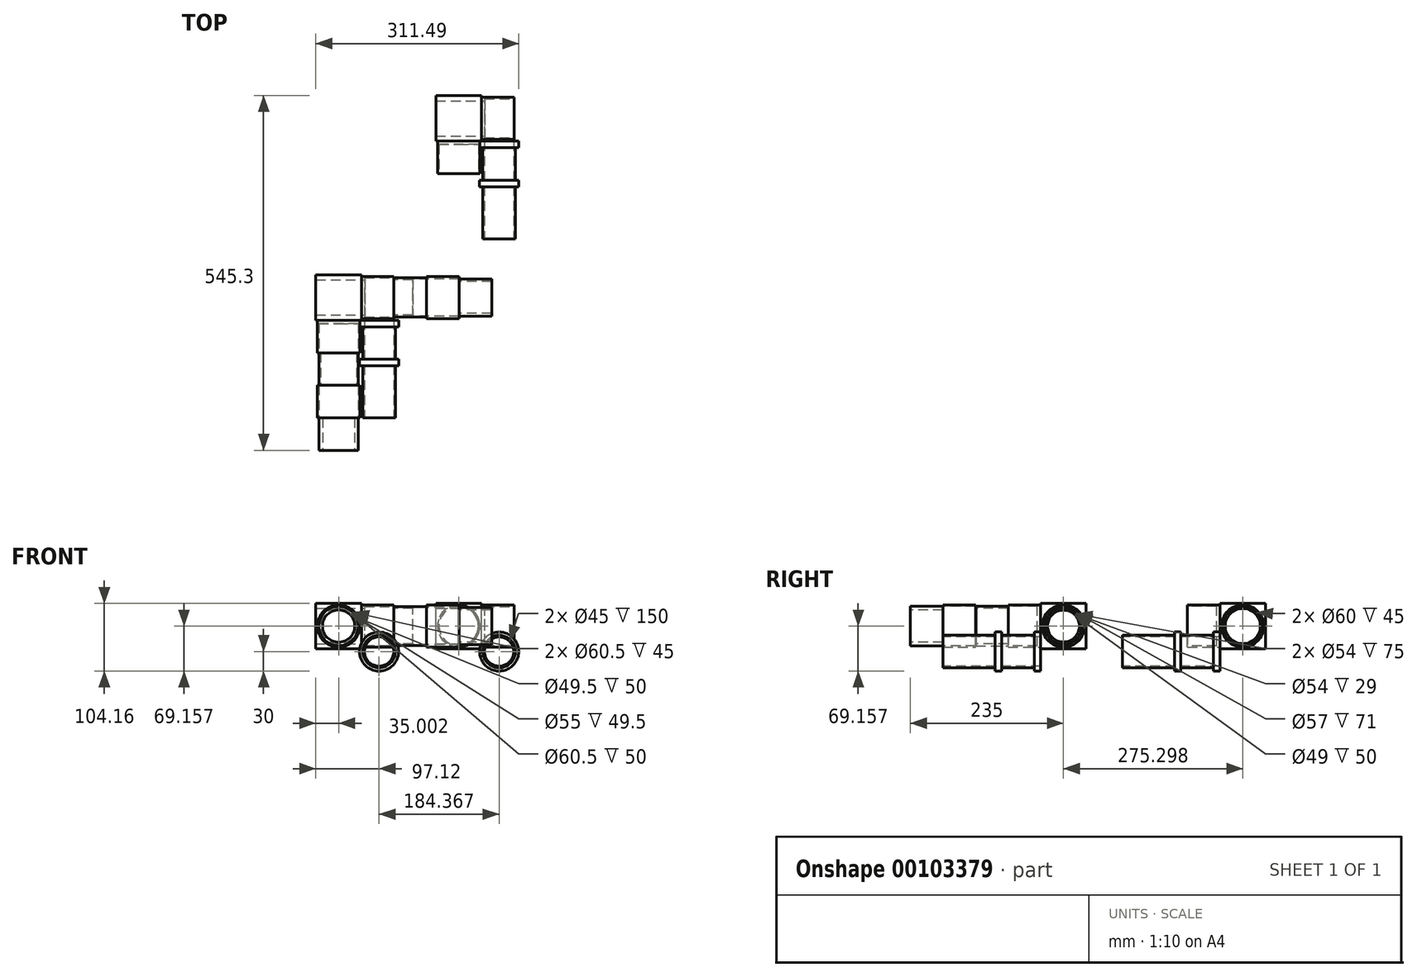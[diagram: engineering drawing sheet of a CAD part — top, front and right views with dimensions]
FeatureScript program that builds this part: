
annotation { "Feature Type Name" : "Feature", "Feature Type Description" : "" }
export const myFeature = defineFeature(function(context is Context, id is Id, definition is map)
    precondition{}
    {
        {
            var Q0;
            Q0=qCreatedBy(makeId("Front.planeOp"),FACE);
            var sketch = newSketch(context, id + "F0", { "sketchPlane" : qUnion([Q0])});
            skCircle(sketch, "E0", {"center": v(0, 0) * mm, "radius": 30 * mm});
            skSolve(sketch);
        }
        {
            var Q0;
            Q0 = qSketchRegion(id + "F0", true);
            extrude(context, id + "F1", {"entities" : qUnion([Q0]), "depth" : 10 * mm});
        }
        {
            var Q0;
            Q0=makeQuery(id+"F1.opExtrude","CAP_FACE",FACE,{"disambiguationData":[OSD([sQuery(id+"F0.wireOp",EDGE,"E0")])],"isStart":false});
            var sketch = newSketch(context, id + "F2", { "sketchPlane" : qUnion([Q0])});
            skCircle(sketch, "E1", {"center": v(0, 0) * mm, "radius": 25 * mm});
            skSolve(sketch);
        }
        {
            var Q0;
            Q0 = qSketchRegion(id + "F2", true);
            extrude(context, id + "F3", {"entities" : qUnion([Q0]), "operationType" : NewBodyOperationType.ADD, "depth" : 50 * mm});
        }
        {
            var Q0;
            Q0=makeQuery(id+"F3.opExtrude","CAP_FACE",FACE,{"disambiguationData":[OSD([sQuery(id+"F2.wireOp",EDGE,"E1")])],"isStart":false});
            var sketch = newSketch(context, id + "F4", { "sketchPlane" : qUnion([Q0])});
            skCircle(sketch, "E2", {"center": v(0, 0) * mm, "radius": 30 * mm});
            skSolve(sketch);
        }
        {
            var Q0;
            Q0 = qSketchRegion(id + "F4", true);
            extrude(context, id + "F5", {"entities" : qUnion([Q0]), "operationType" : NewBodyOperationType.ADD, "depth" : 10 * mm});
        }
        {
            var Q0;
            Q0=makeQuery(id+"F5.opExtrude","CAP_FACE",FACE,{"disambiguationData":[OSD([sQuery(id+"F4.wireOp",EDGE,"E2")])],"isStart":false});
            var sketch = newSketch(context, id + "F6", { "sketchPlane" : qUnion([Q0])});
            skCircle(sketch, "E3", {"center": v(0, 0) * mm, "radius": 25 * mm});
            skSolve(sketch);
        }
        {
            var Q0;
            Q0 = qSketchRegion(id + "F6", true);
            extrude(context, id + "F7", {"entities" : qUnion([Q0]), "operationType" : NewBodyOperationType.ADD, "depth" : 80 * mm});
        }
        {
            var Q0;
            Q0=makeQuery(id+"F7.opExtrude","CAP_FACE",FACE,{"disambiguationData":[OSD([sQuery(id+"F6.wireOp",EDGE,"E3")])],"isStart":false});
            var sketch = newSketch(context, id + "F8", { "sketchPlane" : qUnion([Q0])});
            skCircle(sketch, "E4", {"center": v(0, 0) * mm, "radius": 22.5 * mm});
            skSolve(sketch);
        }
        {
            var Q0;
            Q0 = qSketchRegion(id + "F8", true);
            extrude(context, id + "F9", {"entities" : qUnion([Q0]), "operationType" : NewBodyOperationType.REMOVE, "endBound" : BoundingType.THROUGH_ALL, "oppositeDirection" : true, "depth" : 25 * mm});
        }
        {
            var Q0;
            Q0=qCreatedBy(makeId("Front.planeOp"),FACE);
            var sketch = newSketch(context, id + "F10", { "sketchPlane" : qUnion([Q0])});
            skCircle(sketch, "E5", {"center": v(-62.12, 39.16) * mm, "radius": 32.5 * mm});
            skSolve(sketch);
        }
        {
            var Q0;
            Q0 = qSketchRegion(id + "F10", true);
            extrude(context, id + "F11", {"entities" : qUnion([Q0]), "depth" : 50 * mm});
        }
        {
            var Q0;
            Q0=makeQuery(id+"F11.opExtrude","CAP_FACE",FACE,{"disambiguationData":[OSD([sQuery(id+"F10.wireOp",EDGE,"E5")])],"isStart":false});
            var sketch = newSketch(context, id + "F12", { "sketchPlane" : qUnion([Q0])});
            skCircle(sketch, "E6", {"center": v(-62.12, 39.16) * mm, "radius": 30.25 * mm});
            skSolve(sketch);
        }
        {
            var Q0;
            Q0 = qSketchRegion(id + "F12", true);
            extrude(context, id + "F13", {"entities" : qUnion([Q0]), "operationType" : NewBodyOperationType.REMOVE, "oppositeDirection" : true, "depth" : 45 * mm});
        }
        {
            var Q0;
            Q0=makeQuery(id+"F11.opExtrude","CAP_FACE",FACE,{"disambiguationData":[OSD([sQuery(id+"F10.wireOp",EDGE,"E5")])],"isStart":false});
            var sketch = newSketch(context, id + "F14", { "sketchPlane" : qUnion([Q0])});
            skCircle(sketch, "E7", {"center": v(-62.12, 39.16) * mm, "radius": 30.25 * mm});
            skSolve(sketch);
        }
        {
            var Q0;
            Q0 = qSketchRegion(id + "F14", true);
            extrude(context, id + "F15", {"entities" : qUnion([Q0]), "depth" : 50 * mm});
        }
        {
            var Q0;
            Q0=makeQuery(id+"F15.opExtrude","CAP_FACE",FACE,{"disambiguationData":[OSD([sQuery(id+"F14.wireOp",EDGE,"E7")])],"isStart":false});
            var sketch = newSketch(context, id + "F16", { "sketchPlane" : qUnion([Q0])});
            skCircle(sketch, "E8", {"center": v(-62.12, 39.16) * mm, "radius": 27.5 * mm});
            skSolve(sketch);
        }
        {
            var Q0;
            Q0 = qSketchRegion(id + "F16", true);
            extrude(context, id + "F17", {"entities" : qUnion([Q0]), "operationType" : NewBodyOperationType.REMOVE, "oppositeDirection" : true, "depth" : 55 * mm});
        }
        {
            var Q0;
            Q0=makeQuery(id+"F15.opExtrude","CAP_FACE",FACE,{"disambiguationData":[OSD([sQuery(id+"F14.wireOp",EDGE,"E7")])],"isStart":false});
            var sketch = newSketch(context, id + "F18", { "sketchPlane" : qUnion([Q0])});
            skCircle(sketch, "E9", {"center": v(-62.12, 39.16) * mm, "radius": 32.5 * mm});
            skSolve(sketch);
        }
        {
            var Q0;
            Q0 = qSketchRegion(id + "F18", true);
            extrude(context, id + "F19", {"entities" : qUnion([Q0]), "operationType" : NewBodyOperationType.ADD, "depth" : 50 * mm});
        }
        {
            var Q0;
            Q0=makeQuery(id+"F19.opExtrude","CAP_FACE",FACE,{"disambiguationData":[OSD([sQuery(id+"F18.wireOp",EDGE,"E9")])],"isStart":false});
            var sketch = newSketch(context, id + "F20", { "sketchPlane" : qUnion([Q0])});
            skCircle(sketch, "E10", {"center": v(-62.12, 39.16) * mm, "radius": 30.25 * mm});
            skSolve(sketch);
        }
        {
            var Q0;
            Q0 = qSketchRegion(id + "F20", true);
            extrude(context, id + "F21", {"entities" : qUnion([Q0]), "operationType" : NewBodyOperationType.REMOVE, "oppositeDirection" : true, "depth" : 50.5 * mm});
        }
        {
            var Q0;
            Q0=makeQuery(id+"F19.opExtrude","CAP_FACE",FACE,{"disambiguationData":[OSD([sQuery(id+"F18.wireOp",EDGE,"E9")])],"isStart":false});
            var sketch = newSketch(context, id + "F22", { "sketchPlane" : qUnion([Q0])});
            skCircle(sketch, "E11", {"center": v(-62.12, 39.16) * mm, "radius": 30.25 * mm});
            skSolve(sketch);
        }
        {
            var Q0;
            Q0 = qSketchRegion(id + "F22", true);
            extrude(context, id + "F23", {"entities" : qUnion([Q0]), "depth" : 50 * mm});
        }
        {
            var Q0;
            Q0=makeQuery(id+"F23.opExtrude","CAP_FACE",FACE,{"disambiguationData":[OSD([sQuery(id+"F22.wireOp",EDGE,"E11")])],"isStart":false});
            var sketch = newSketch(context, id + "F24", { "sketchPlane" : qUnion([Q0])});
            skCircle(sketch, "E12", {"center": v(-62.12, 39.16) * mm, "radius": 24.75 * mm});
            skSolve(sketch);
        }
        {
            var Q0;
            Q0 = qSketchRegion(id + "F24", true);
            extrude(context, id + "F25", {"entities" : qUnion([Q0]), "operationType" : NewBodyOperationType.REMOVE, "oppositeDirection" : true, "depth" : 51 * mm});
        }
        {
            var Q0;
            Q0=makeQuery(id+"F11.opExtrude","CAP_FACE",FACE,{"disambiguationData":[OSD([sQuery(id+"F10.wireOp",EDGE,"E5")])],"isStart":true});
            var sketch = newSketch(context, id + "F26", { "sketchPlane" : qUnion([Q0])});
            skLineSegment(sketch, "E13.bottom", {"start": v(97.12, 4.16) * mm, "end": v(27.12, 4.16) * mm});
            skLineSegment(sketch, "E13.top", {"start": v(97.12, 74.16) * mm, "end": v(27.12, 74.16) * mm});
            skLineSegment(sketch, "E13.left", {"start": v(97.12, 4.16) * mm, "end": v(97.12, 74.16) * mm});
            skLineSegment(sketch, "E13.right", {"start": v(27.12, 4.16) * mm, "end": v(27.12, 74.16) * mm});
            skPoint(sketch, "E13.middle", {"position": v(62.12, 39.16) * mm});
            skSolve(sketch);
        }
        {
            var Q0;
            Q0 = qSketchRegion(id + "F26", true);
            extrude(context, id + "F27", {"entities" : qUnion([Q0]), "operationType" : NewBodyOperationType.ADD, "depth" : 70 * mm});
        }
        {
            var Q0;
            Q0=makeQuery(id+"F27.opExtrude","SWEPT_FACE",FACE,{"disambiguationData":[OSD([sQuery(id+"F26.wireOp",EDGE,"E13.right")])]});
            var sketch = newSketch(context, id + "F28", { "sketchPlane" : qUnion([Q0])});
            skCircle(sketch, "E14", {"center": v(35, 39.16) * mm, "radius": 32.5 * mm});
            skPoint(sketch, "E15", {"position": v(70, 39.16) * mm});
            skPoint(sketch, "E16", {"position": v(35, 4.16) * mm});
            skSolve(sketch);
        }
        {
            var Q0;
            Q0 = qSketchRegion(id + "F28", true);
            extrude(context, id + "F29", {"entities" : qUnion([Q0]), "operationType" : NewBodyOperationType.ADD, "depth" : 50 * mm});
        }
        {
            var Q0;
            Q0=makeQuery(id+"F29.opExtrude","CAP_FACE",FACE,{"disambiguationData":[OSD([sQuery(id+"F28.wireOp",EDGE,"E14")])],"isStart":false});
            var sketch = newSketch(context, id + "F30", { "sketchPlane" : qUnion([Q0])});
            skCircle(sketch, "E17", {"center": v(35, 39.16) * mm, "radius": 30 * mm});
            skSolve(sketch);
        }
        {
            var Q0;
            Q0 = qSketchRegion(id + "F30", true);
            extrude(context, id + "F31", {"entities" : qUnion([Q0]), "operationType" : NewBodyOperationType.REMOVE, "oppositeDirection" : true, "depth" : 45 * mm});
        }
        {
            var Q0;
            Q0=makeQuery(id+"F29.opExtrude","CAP_FACE",FACE,{"disambiguationData":[OSD([sQuery(id+"F28.wireOp",EDGE,"E14")])],"isStart":false});
            var sketch = newSketch(context, id + "F32", { "sketchPlane" : qUnion([Q0])});
            skCircle(sketch, "E18", {"center": v(35, 39.16) * mm, "radius": 30 * mm});
            skSolve(sketch);
        }
        {
            var Q0;
            Q0 = qSketchRegion(id + "F32", true);
            extrude(context, id + "F33", {"entities" : qUnion([Q0]), "depth" : 50 * mm});
        }
        {
            var Q0;
            Q0=makeQuery(id+"F33.opExtrude","CAP_FACE",FACE,{"disambiguationData":[OSD([sQuery(id+"F32.wireOp",EDGE,"E18")])],"isStart":false});
            shell(context, id + "F34", {"entities" : qUnion([Q0]), "thickness" : 3 * mm});
        }
        {
            var Q0;
            {var subQ0=sQuery(id+"F32.wireOp",EDGE,"E18");Q0=makeQuery(id+"F34.opShell","OFFSET_FACE",FACE,{"disambiguationData":[OSD([subQ0]),TDD([makeQuery(id+"F33.opExtrude","CAP_FACE",FACE,{"disambiguationData":[OSD([subQ0])],"isStart":true})])]});}
            extrude(context, id + "F35", {"entities" : qUnion([Q0]), "operationType" : NewBodyOperationType.REMOVE, "endBound" : BoundingType.THROUGH_ALL, "oppositeDirection" : true, "depth" : 25 * mm});
        }
        {
            var Q0;
            Q0=makeQuery(id+"F33.opExtrude","CAP_FACE",FACE,{"disambiguationData":[OSD([sQuery(id+"F32.wireOp",EDGE,"E18")])],"isStart":false});
            var sketch = newSketch(context, id + "F36", { "sketchPlane" : qUnion([Q0])});
            skCircle(sketch, "E19", {"center": v(35, 39.16) * mm, "radius": 32.5 * mm});
            skSolve(sketch);
        }
        {
            var Q0;
            Q0 = qSketchRegion(id + "F36", true);
            extrude(context, id + "F37", {"entities" : qUnion([Q0]), "operationType" : NewBodyOperationType.ADD, "depth" : 50 * mm});
        }
        {
            var Q0;
            Q0=makeQuery(id+"F37.opExtrude","CAP_FACE",FACE,{"disambiguationData":[OSD([sQuery(id+"F36.wireOp",EDGE,"E19")])],"isStart":false});
            shell(context, id + "F38", {"entities" : qUnion([Q0]), "thickness" : 4 * mm});
        }
        {
            var Q0;
            {var subQ0=sQuery(id+"F32.wireOp",EDGE,"E18");var subQ1=makeQuery(id+"F33.opExtrude","SWEPT_FACE",FACE,{"disambiguationData":[OSD([subQ0])]});var subQ2=sQuery(id+"F36.wireOp",EDGE,"E19");var subQ3=makeQuery(id+"F37.opExtrude","CAP_FACE",FACE,{"disambiguationData":[OSD([subQ2])],"isStart":true});Q0=makeQuery(id+"F38.opShell","OFFSET_FACE",FACE,{"disambiguationData":[OSD([subQ2]),TDD([makeQuery(id+"F37.boolean.opBoolean","SPLIT",FACE,{"disambiguationData":[TD([subQ1])],"derivedFrom":subQ3}),makeQuery(id+"F37.boolean.opBoolean","SPLIT",FACE,{"disambiguationData":[TD([makeQuery(id+"F35.opExtrude","SWEPT_FACE",FACE,{"disambiguationData":[OSD([subQ0])]})])],"derivedFrom":subQ3})])]});}
            extrude(context, id + "F39", {"entities" : qUnion([Q0]), "operationType" : NewBodyOperationType.REMOVE, "oppositeDirection" : true, "depth" : 25 * mm});
        }
        {
            var Q0;
            Q0=makeQuery(id+"F37.opExtrude","CAP_FACE",FACE,{"disambiguationData":[OSD([sQuery(id+"F36.wireOp",EDGE,"E19")])],"isStart":false});
            var sketch = newSketch(context, id + "F40", { "sketchPlane" : qUnion([Q0])});
            skCircle(sketch, "E20", {"center": v(35, 39.16) * mm, "radius": 28.5 * mm});
            skSolve(sketch);
        }
        {
            var Q0;
            Q0 = qSketchRegion(id + "F40", true);
            extrude(context, id + "F41", {"entities" : qUnion([Q0]), "depth" : 50 * mm});
        }
        {
            var Q0;
            Q0=makeQuery(id+"F41.opExtrude","CAP_FACE",FACE,{"disambiguationData":[OSD([sQuery(id+"F40.wireOp",EDGE,"E20")])],"isStart":false});
            shell(context, id + "F42", {"entities" : qUnion([Q0]), "thickness" : 4 * mm});
        }
        {
            var Q0;
            {var subQ0=sQuery(id+"F40.wireOp",EDGE,"E20");Q0=makeQuery(id+"F42.opShell","OFFSET_FACE",FACE,{"disambiguationData":[OSD([subQ0]),TDD([makeQuery(id+"F41.opExtrude","CAP_FACE",FACE,{"disambiguationData":[OSD([subQ0])],"isStart":true})])]});}
            extrude(context, id + "F43", {"entities" : qUnion([Q0]), "operationType" : NewBodyOperationType.REMOVE, "endBound" : BoundingType.UP_TO_NEXT, "oppositeDirection" : true, "depth" : 25 * mm});
        }
        {
            var Q0;
            Q0=makeQuery(id+"F1.opExtrude","SWEPT_BODY",BODY,{"disambiguationData":[OSD([sQuery(id+"F0.wireOp",EDGE,"E0")])]});
            transform(context, id + "F44", {"entities" : qUnion([Q0]), "transformType" : TransformType.TRANSLATION_3D, "dx" : 184.37 * mm, "dy" : 275.3 * mm, "dz" : 0 * mm, "makeCopy" : true});
        }
    });
